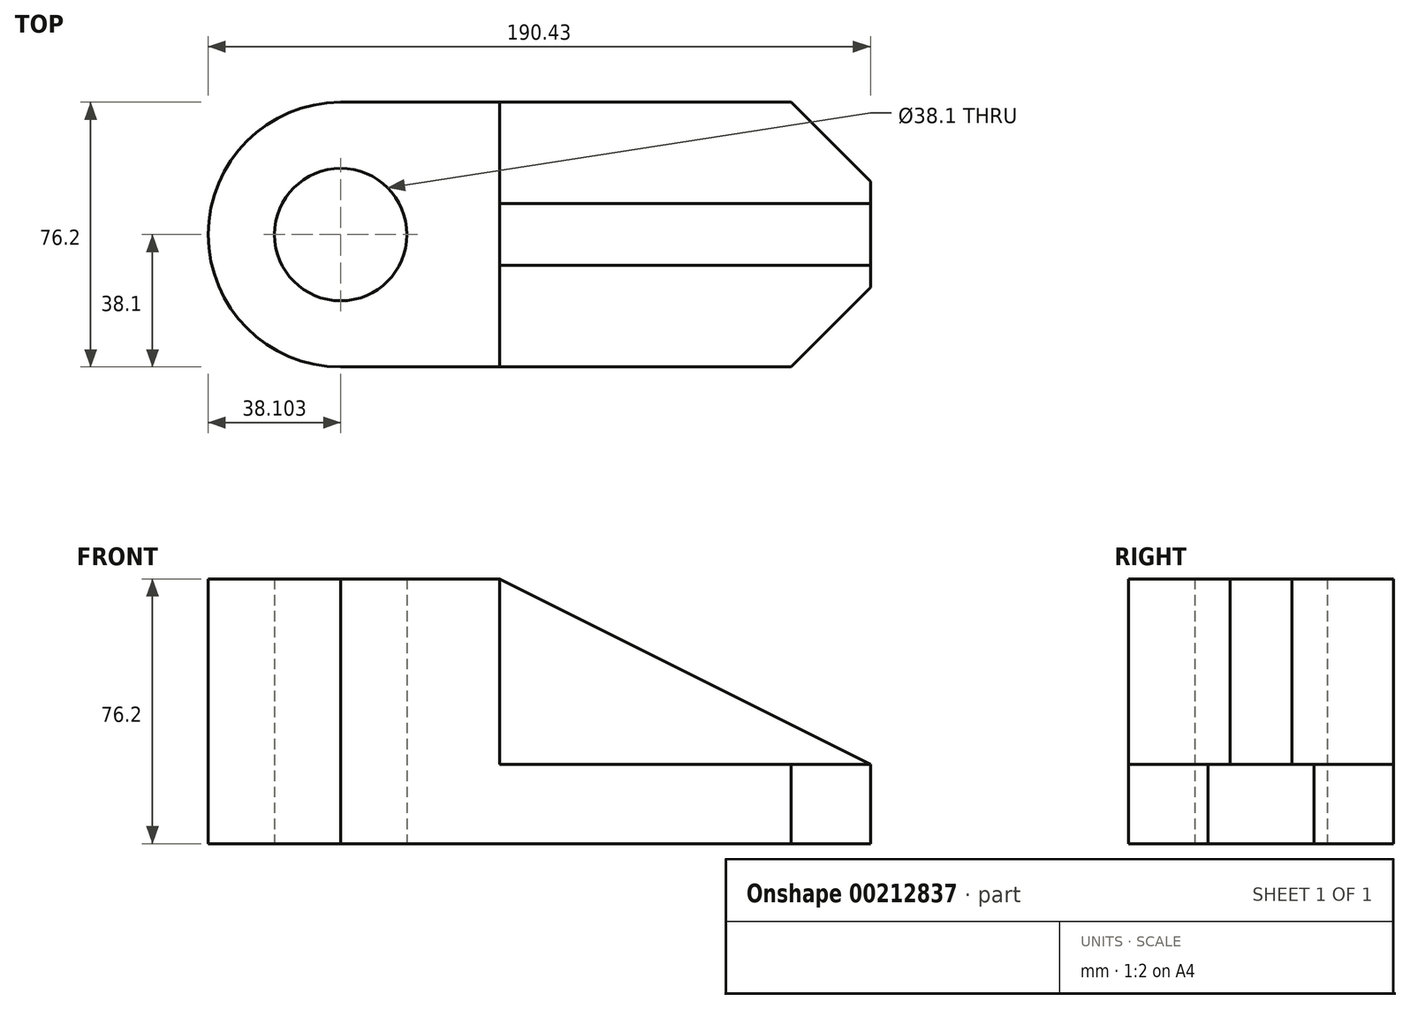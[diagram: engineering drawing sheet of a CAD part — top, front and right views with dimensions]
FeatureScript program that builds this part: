
annotation { "Feature Type Name" : "Feature", "Feature Type Description" : "" }
export const myFeature = defineFeature(function(context is Context, id is Id, definition is map)
    precondition{}
    {
        {
            var Q0;
            Q0=qCreatedBy(makeId("Front.planeOp"),FACE);
            var sketch = newSketch(context, id + "F0", { "sketchPlane" : qUnion([Q0])});
            skLineSegment(sketch, "E0", {"start": v(-71.27, 0) * mm, "end": v(58.27, 0) * mm});
            skLineSegment(sketch, "E1", {"start": v(58.27, 0) * mm, "end": v(81.13, 0) * mm});
            skLineSegment(sketch, "E2", {"start": v(-71.27, 0) * mm, "end": v(-71.27, 76.2) * mm});
            skLineSegment(sketch, "E3", {"start": v(-71.27, 76.2) * mm, "end": v(-25.55, 76.2) * mm});
            skLineSegment(sketch, "E4", {"start": v(81.13, 0) * mm, "end": v(81.13, 22.86) * mm});
            skLineSegment(sketch, "E5", {"start": v(81.13, 22.86) * mm, "end": v(-25.55, 22.86) * mm});
            skLineSegment(sketch, "E6", {"start": v(-25.55, 22.86) * mm, "end": v(-25.55, 76.2) * mm});
            skLineSegment(sketch, "E7", {"start": v(81.13, 22.86) * mm, "end": v(-25.55, 76.2) * mm});
            skLineSegment(sketch, "E8", {"start": v(-71.27, 0) * mm, "end": v(-109.37, 0) * mm});
            skLineSegment(sketch, "E9", {"start": v(-71.27, 76.2) * mm, "end": v(-109.37, 76.2) * mm});
            skLineSegment(sketch, "E10", {"start": v(-109.37, 76.2) * mm, "end": v(-109.37, 0) * mm});
            skSolve(sketch);
        }
        {
            var Q0;
            Q0=makeQuery(id+"F0.imprint","IMPRINT",FACE,{"disambiguationData":[TD([[makeQuery(id+"F0.imprint","IMPRINT",EDGE,{"derivedFrom":sQuery(id+"F0.wireOp",EDGE,"E0")}),1.0]])]});
            extrude(context, id + "F1", {"entities" : qUnion([Q0]), "endBound" : BoundingType.SYMMETRIC, "depth" : 76.2 * mm});
        }
        {
            var Q0;
            Q0=makeQuery(id+"F0.imprint","IMPRINT",FACE,{"disambiguationData":[TD([[makeQuery(id+"F0.imprint","IMPRINT",EDGE,{"derivedFrom":sQuery(id+"F0.wireOp",EDGE,"E5")}),-1.0]])]});
            extrude(context, id + "F2", {"entities" : qUnion([Q0]), "endBound" : BoundingType.SYMMETRIC, "depth" : 17.78 * mm});
        }
        {
            var Q0;
            Q0=makeQuery(id+"F1.opExtrude","CAP_EDGE",EDGE,{"disambiguationData":[OSD([sQuery(id+"F0.wireOp",EDGE,"E4")])],"isStart":false});
            var Q1;
            Q1=makeQuery(id+"F1.opExtrude","CAP_EDGE",EDGE,{"disambiguationData":[OSD([sQuery(id+"F0.wireOp",EDGE,"E4")])],"isStart":true});
            chamfer(context, id + "F3", {"entities" : qUnion([Q0, Q1]), "width" : 22.86 * mm, "tangentPropagation" : true});
        }
        {
            var Q0;
            Q0=qCreatedBy(makeId("Top.planeOp"),FACE);
            var sketch = newSketch(context, id + "F4", { "sketchPlane" : qUnion([Q0])});
            skArc(sketch, "E11", {"start": v(-71.2, 19.05) * mm, "mid": v(-90.25, 0) * mm, "end": v(-71.2, -19.05) * mm});
            skArc(sketch, "E12", {"start": v(-71.2, 38.1) * mm, "mid": v(-109.3, 0) * mm, "end": v(-71.2, -38.1) * mm});
            skLineSegment(sketch, "E13", {"start": v(-71.2, 19.05) * mm, "end": v(-71.2, 38.1) * mm});
            skLineSegment(sketch, "E14", {"start": v(-71.2, -19.05) * mm, "end": v(-71.2, -38.1) * mm});
            skSolve(sketch);
        }
        {
            var Q0;
            Q0=makeQuery(id+"F4.imprint","IMPRINT",FACE,{"disambiguationData":[TD([[makeQuery(id+"F4.imprint","IMPRINT",EDGE,{"derivedFrom":sQuery(id+"F4.wireOp",EDGE,"E11")}),-1.0]])]});
            extrude(context, id + "F5", {"entities" : qUnion([Q0]), "operationType" : NewBodyOperationType.ADD, "depth" : 76.2 * mm});
        }
        {
            var Q0;
            Q0=sQuery(id+"F4.wireOp",VERTEX,"E12.center");
            var Q1;
            Q1=makeQuery(id+"F1.opExtrude","SWEPT_BODY",BODY,{"disambiguationData":[OSD([sQuery(id+"F0.wireOp",EDGE,"E0"),sQuery(id+"F0.wireOp",EDGE,"E1"),sQuery(id+"F0.wireOp",EDGE,"E2"),sQuery(id+"F0.wireOp",EDGE,"E3"),sQuery(id+"F0.wireOp",EDGE,"E4"),sQuery(id+"F0.wireOp",EDGE,"E5"),sQuery(id+"F0.wireOp",EDGE,"E6")])]});
            hole(context, id + "F6", {"style" : HoleStyle.SIMPLE, "endStyle" : HoleEndStyle.THROUGH, "oppositeDirection" : true, "holeDiameter" : 38.1 * mm, "locations" : qUnion([Q0]), "scope" : qUnion([Q1]), "isTappedThrough" : true});
        }
    });
